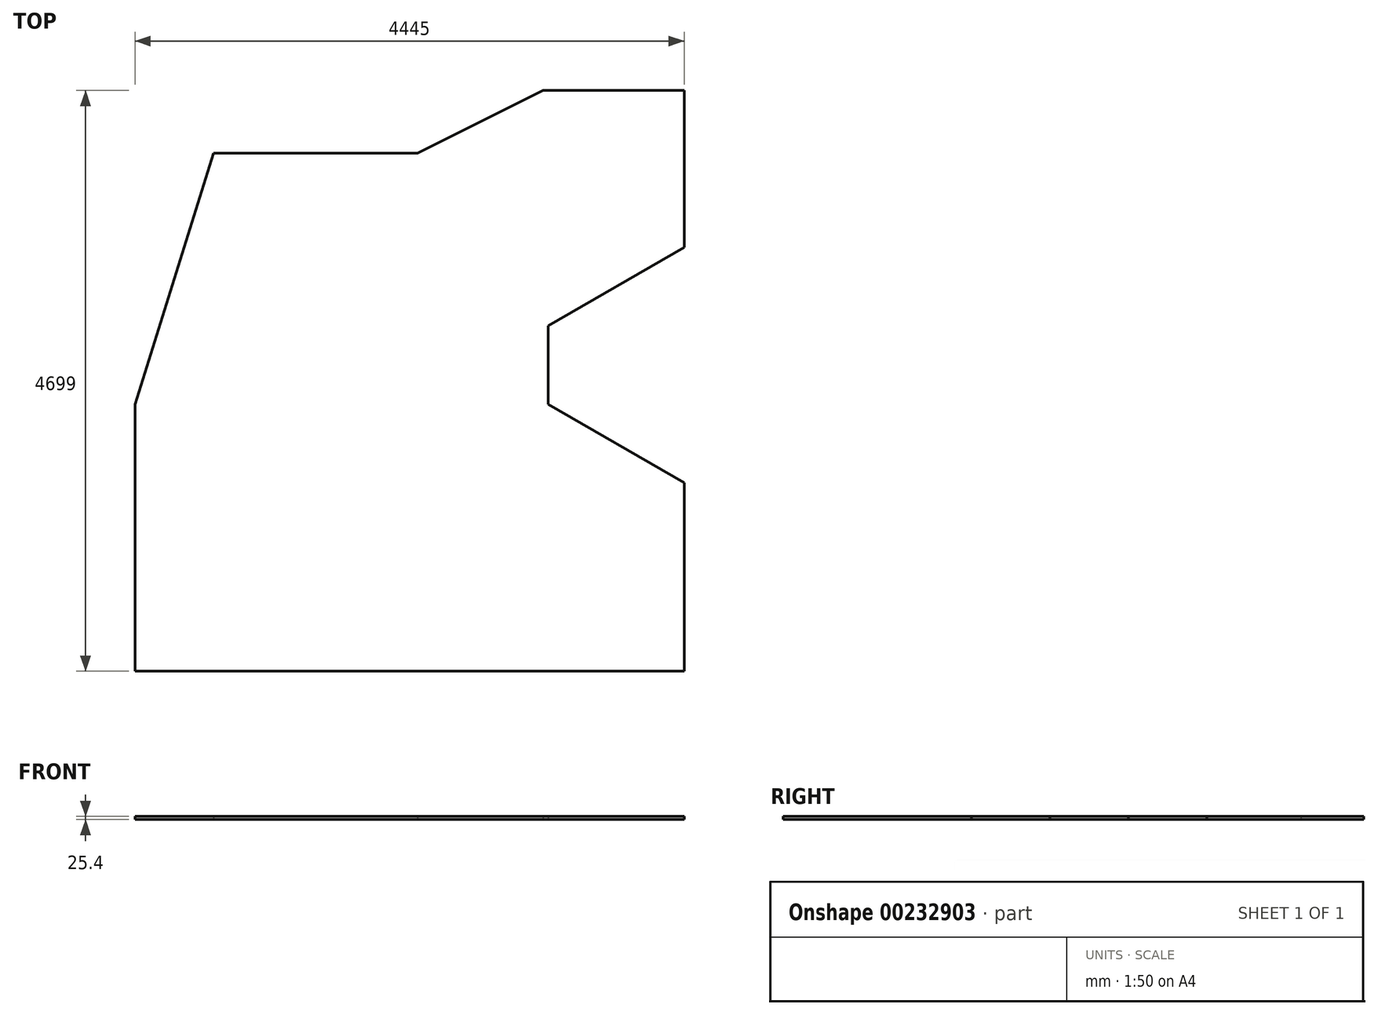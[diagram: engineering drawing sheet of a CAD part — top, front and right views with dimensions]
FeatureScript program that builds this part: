
annotation { "Feature Type Name" : "Feature", "Feature Type Description" : "" }
export const myFeature = defineFeature(function(context is Context, id is Id, definition is map)
    precondition{}
    {
        {
            var Q0;
            Q0=qCreatedBy(makeId("Top.planeOp"),FACE);
            var sketch = newSketch(context, id + "F0", { "sketchPlane" : qUnion([Q0])});
            skLineSegment(sketch, "E0", {"start": v(-2140.3, -282.32) * mm, "end": v(2304.7, -282.32) * mm});
            skLineSegment(sketch, "E1", {"start": v(-2140.3, -282.32) * mm, "end": v(-2140.3, 1876.68) * mm});
            skLineSegment(sketch, "E2", {"start": v(-2140.3, 1876.68) * mm, "end": v(-1505.3, 3908.68) * mm});
            skLineSegment(sketch, "E3", {"start": v(-1505.3, 3908.68) * mm, "end": v(145.7, 3908.68) * mm});
            skLineSegment(sketch, "E4", {"start": v(145.7, 3908.68) * mm, "end": v(1161.7, 4416.68) * mm});
            skLineSegment(sketch, "E5", {"start": v(1161.7, 4416.68) * mm, "end": v(2304.7, 4416.68) * mm});
            skLineSegment(sketch, "E6", {"start": v(2304.7, 4416.68) * mm, "end": v(2304.7, 3146.68) * mm});
            skLineSegment(sketch, "E7", {"start": v(2304.7, 3146.68) * mm, "end": v(1204.85, 2511.68) * mm});
            skLineSegment(sketch, "E8", {"start": v(1204.85, 2511.68) * mm, "end": v(1204.85, 1876.68) * mm});
            skLineSegment(sketch, "E9", {"start": v(2304.7, -282.32) * mm, "end": v(2304.7, 1241.68) * mm});
            skLineSegment(sketch, "E10", {"start": v(1204.85, 1876.68) * mm, "end": v(2304.7, 1241.68) * mm});
            skSolve(sketch);
        }
        {
            var Q0;
            Q0 = qSketchRegion(id + "F0", true);
            extrude(context, id + "F1", {"entities" : qUnion([Q0]), "depth" : 25.4 * mm});
        }
    });
